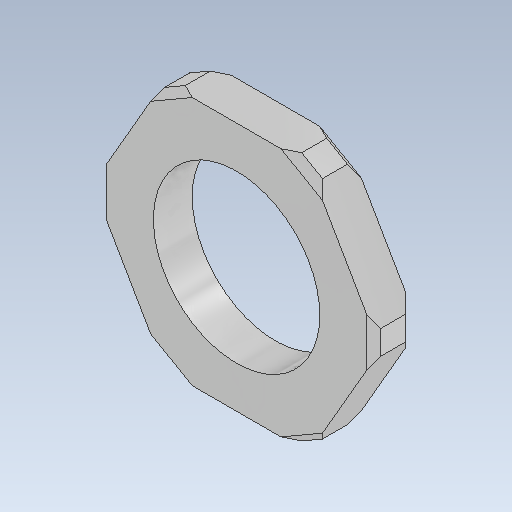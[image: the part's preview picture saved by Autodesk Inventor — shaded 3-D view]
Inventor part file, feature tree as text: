
AUTODESK INVENTOR PART (.ipt)
format: ipt  version: 2021 (Build 250183000, 183)  size: 139,264 bytes
history: native  units: mm
features: extrude x2, chamfer x2, sketch x2
ambient origin geometry x8: Origin, YZ Plane, XZ Plane, XY Plane, X Axis, Y Axis, Z Axis, Center Point
bodies: Solid1 (feature_tree)
feature tree (6):
  extrude  "Extrusion1"  Depth=2.8mm TaperAngle=0.0deg
  extrude  "Extrusion2"  Depth=2.8mm TaperAngle=0.0deg
  chamfer  "Chamfer1"  Distance=1.0mm Angle=45.0deg
  chamfer  "Chamfer2"  Distance=0.5mm Angle=45.0deg
  sketch  "Sketch1"  dims[d0=18.0mm d1=2.8mm d2=0.0mm]
  sketch  "Sketch2"  dims[d3=12.0mm d4=2.8mm d5=0.0mm d6=1.0mm d7=2.0mm d8=45.0deg d9=0.5mm d10=2.0mm d11=45.0deg]
